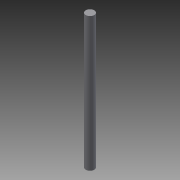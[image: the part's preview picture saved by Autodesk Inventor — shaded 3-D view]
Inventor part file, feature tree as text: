
AUTODESK INVENTOR PART (.ipt)
format: ipt  version: 2014 (Build 180170000, 170)  size: 62,464 bytes
history: native  units: in
note: dims shown in document units (in); Inventor stores cm internally (conversion verified against a paired STEP export)
features: extrude x1, sketch x1
ambient origin geometry x8: Origin, YZ Plane, XZ Plane, XY Plane, X Axis, Y Axis, Z Axis, Center Point
bodies: Solid1 (feature_tree)
feature tree (2):
  extrude  "Extrusion1"  Depth=3.0in TaperAngle=0.0deg
  sketch  "Sketch1"  dims[d0=0.19in d1=3.0in d2=0.0in]
